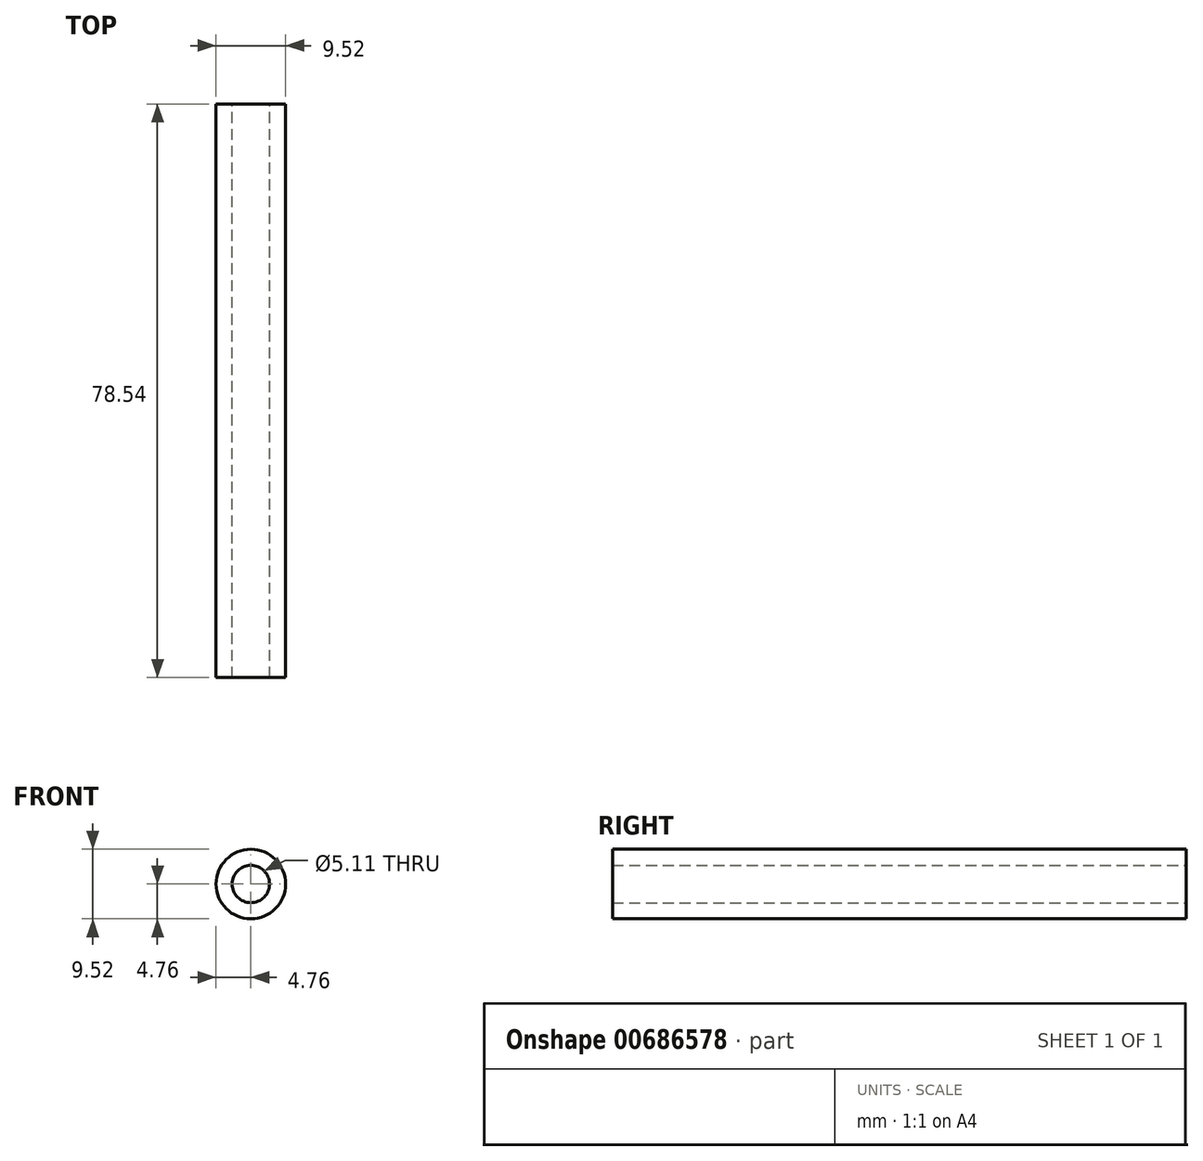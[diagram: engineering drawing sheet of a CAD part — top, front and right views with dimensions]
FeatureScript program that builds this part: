
annotation { "Feature Type Name" : "Feature", "Feature Type Description" : "" }
export const myFeature = defineFeature(function(context is Context, id is Id, definition is map)
    precondition{}
    {
        {
            var Q0;
            Q0=qCreatedBy(makeId("Front.planeOp"),FACE);
            var sketch = newSketch(context, id + "F0", { "sketchPlane" : qUnion([Q0])});
            skCircle(sketch, "E0", {"center": v(0, 0) * mm, "radius": 2.55 * mm});
            skCircle(sketch, "E1", {"center": v(0, 0) * mm, "radius": 4.76 * mm});
            skSolve(sketch);
        }
        {
            var Q0;
            Q0=makeQuery(id+"F0.imprint","IMPRINT",FACE,{"disambiguationData":[TD([[makeQuery(id+"F0.imprint","IMPRINT",EDGE,{"derivedFrom":sQuery(id+"F0.wireOp",EDGE,"E0")}),-1.0]])]});
            extrude(context, id + "F1", {"entities" : qUnion([Q0]), "endBound" : BoundingType.SYMMETRIC, "depth" : 78.53 * mm, "offsetDistance" : 25.4 * mm});
        }
    });
